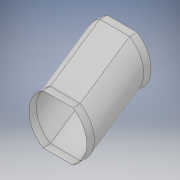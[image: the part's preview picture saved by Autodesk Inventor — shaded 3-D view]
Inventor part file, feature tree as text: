
AUTODESK INVENTOR PART (.ipt)
format: ipt  version: 2017 (Build 210142000, 142)  size: 158,208 bytes
history: native  units: in
note: dims shown in document units (in); Inventor stores cm internally (conversion verified against a paired STEP export)
features: sketch x2, extrude x2, plane x1, sweep x1, delete_face x1
ambient origin geometry x8: Origin, YZ Plane, XZ Plane, XY Plane, X Axis, Y Axis, Z Axis, Center Point
bodies: Solid1 (feature_tree)
feature tree (7):
  sketch  "Sketch1"  dims[d0=6.6667in d3=1.0in d4=0.0in d12=8.0in]
  extrude  "connection top"  Depth=8.0in
  plane  "Work Plane2"
  sweep  "ramp"
  extrude  "connection bottom"  Depth=3.8873in TaperAngle=0.0deg
  delete_face  "Delete Face1"
  sketch  "Sketch6"  dims[d28=8.0in d45=0.0in d46=0.0in d49=1.0in d50=0.0in d70=0.8521in d87=4.0in d89=3.8873in d90=3.8873in d94=1.6458in d100=3.3333in d102=4.0in d104=3.8873in d105=3.8873in d109=1.6458in d115=3.3333in]
